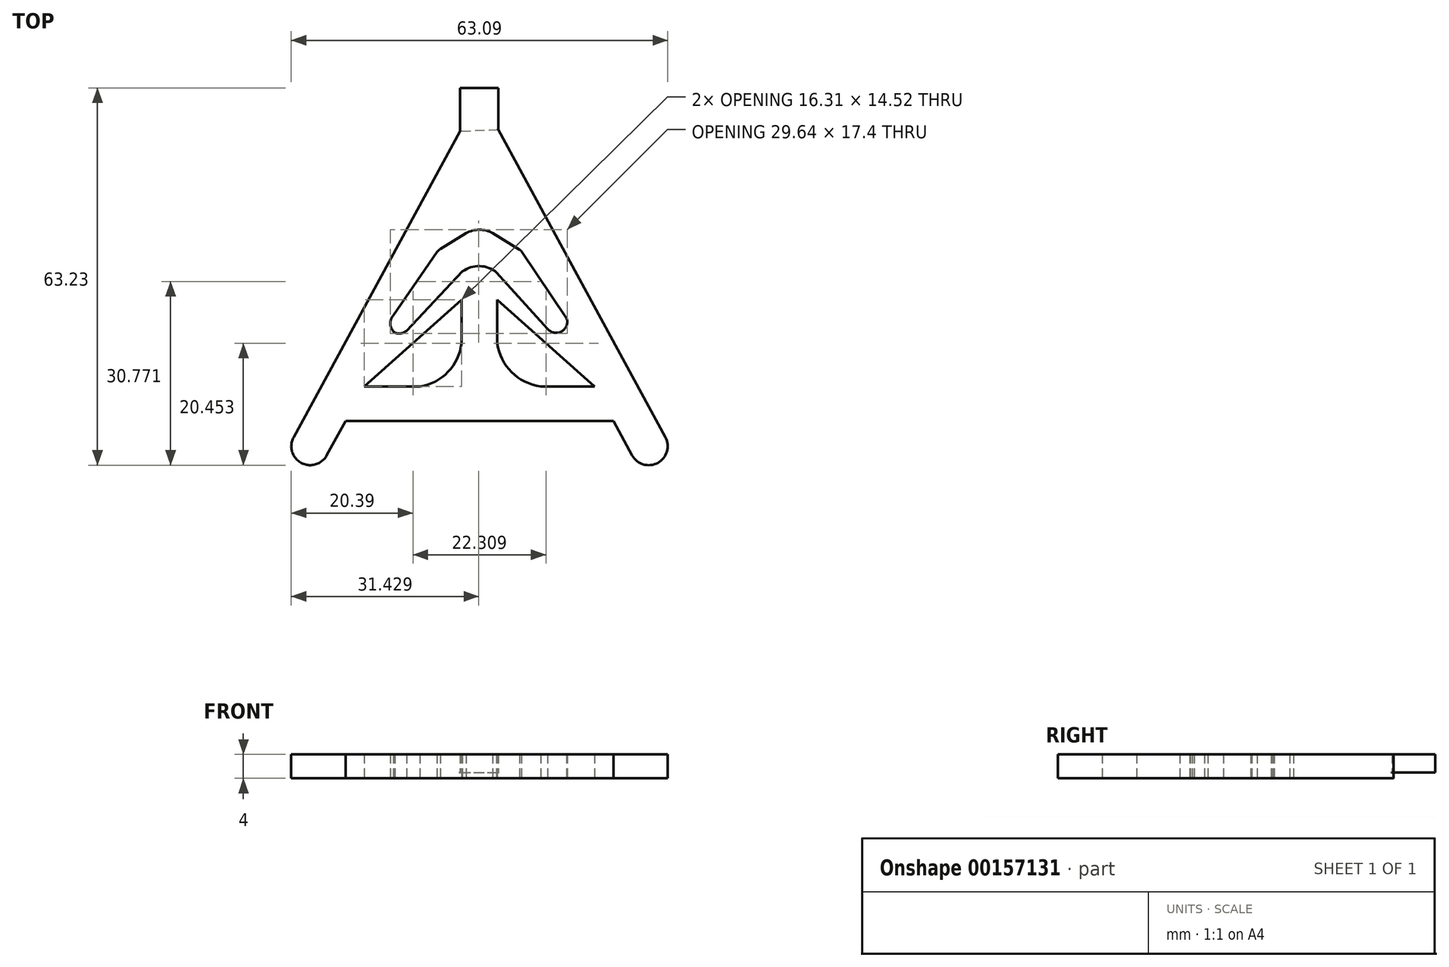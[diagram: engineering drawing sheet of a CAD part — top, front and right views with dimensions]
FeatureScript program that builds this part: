
annotation { "Feature Type Name" : "Feature", "Feature Type Description" : "" }
export const myFeature = defineFeature(function(context is Context, id is Id, definition is map)
    precondition{}
    {
        {
            var Q0;
            Q0=qCreatedBy(makeId("Top.planeOp"),FACE);
            var sketch = newSketch(context, id + "F0", { "sketchPlane" : qUnion([Q0])});
            skLineSegment(sketch, "E0", {"start": v(-31.15, 0) * mm, "end": v(-3.28, 51.3) * mm});
            skLineSegment(sketch, "E1", {"start": v(3.14, 51.54) * mm, "end": v(31.17, 0) * mm});
            skLineSegment(sketch, "E2.top", {"start": v(-3.28, 58.54) * mm, "end": v(3.14, 58.54) * mm});
            skLineSegment(sketch, "E2.left", {"start": v(-3.28, 51.3) * mm, "end": v(-3.28, 58.54) * mm});
            skLineSegment(sketch, "E2.right", {"start": v(3.14, 51.54) * mm, "end": v(3.14, 58.54) * mm});
            skPoint(sketch, "E3.orphan", {"position": v(0, 57.32) * mm});
            skLineSegment(sketch, "E4.0", {"start": v(19.31, 8.5) * mm, "end": v(25.59, -3.03) * mm});
            skLineSegment(sketch, "E4.1", {"start": v(-25.57, -3.03) * mm, "end": v(-19.3, 8.5) * mm});
            skLineSegment(sketch, "E5", {"start": v(-19.3, 8.5) * mm, "end": v(-3, 23.02) * mm});
            skLineSegment(sketch, "E6", {"start": v(3, 23.02) * mm, "end": v(19.31, 8.5) * mm});
            skPoint(sketch, "E7.start.orphan", {"position": v(-6.9, 31.34) * mm});
            skPoint(sketch, "E8.end.orphan", {"position": v(0, 35.55) * mm});
            skPoint(sketch, "E9.orphan", {"position": v(6.9, 31.34) * mm});
            skArc(sketch, "E10", {"start": v(-31.15, 0) * mm, "mid": v(-29.88, -4.3) * mm, "end": v(-25.57, -3.03) * mm});
            skArc(sketch, "E11", {"start": v(25.59, -3.03) * mm, "mid": v(29.9, -4.3) * mm, "end": v(31.17, 0) * mm});
            skLineSegment(sketch, "E12", {"start": v(-19.3, 8.5) * mm, "end": v(-9.98, 8.5) * mm});
            skLineSegment(sketch, "E13", {"start": v(22.45, 2.74) * mm, "end": v(-22.44, 2.74) * mm});
            skLineSegment(sketch, "E14", {"start": v(-3, 23.02) * mm, "end": v(-3, 15.76) * mm});
            skLineSegment(sketch, "E15", {"start": v(3, 23.02) * mm, "end": v(3, 15.76) * mm});
            skLineSegment(sketch, "E16", {"start": v(-7.1, 31.05) * mm, "end": v(-14.72, 20) * mm});
            skPoint(sketch, "E16.endSnap0", {"position": v(-9.65, 17.1) * mm});
            skLineSegment(sketch, "E17", {"start": v(-12.23, 17.86) * mm, "end": v(-2.84, 27.8) * mm});
            skLineSegment(sketch, "E18", {"start": v(2.88, 27.62) * mm, "end": v(11.53, 18.05) * mm});
            skPoint(sketch, "E18.endSnap0", {"position": v(9.66, 17.1) * mm});
            skLineSegment(sketch, "E19", {"start": v(14.62, 19.9) * mm, "end": v(7.02, 31.16) * mm});
            skLineSegment(sketch, "E20", {"start": v(2.23, 34.19) * mm, "end": v(6.75, 31.43) * mm});
            skLineSegment(sketch, "E21", {"start": v(-6.56, 31.54) * mm, "end": v(-2.24, 34.18) * mm});
            skPoint(sketch, "E22.orphan", {"position": v(0, 25.7) * mm});
            skArc(sketch, "E23", {"start": v(-9.98, 8.5) * mm, "mid": v(-5.25, 10.94) * mm, "end": v(-3, 15.76) * mm});
            skArc(sketch, "E24", {"start": v(3, 15.76) * mm, "mid": v(5.4, 10.9) * mm, "end": v(10.27, 8.5) * mm});
            skPoint(sketch, "E25.orphan", {"position": v(-3, 8.5) * mm});
            skPoint(sketch, "E26.orphan", {"position": v(3, 8.5) * mm});
            skLineSegment(sketch, "E27.trimOffspring", {"start": v(10.27, 8.5) * mm, "end": v(19.31, 8.5) * mm});
            skArc(sketch, "E28", {"start": v(-14.44, 20.41) * mm, "mid": v(-14.93, 18.9) * mm, "end": v(-14.16, 17.5) * mm});
            skArc(sketch, "E29", {"start": v(-14.16, 17.5) * mm, "mid": v(-13.15, 17.41) * mm, "end": v(-12.23, 17.86) * mm});
            skPoint(sketch, "E30.orphan", {"position": v(-16.72, 17.1) * mm});
            skArc(sketch, "E31", {"start": v(11.44, 18.14) * mm, "mid": v(13.75, 17.72) * mm, "end": v(14.62, 19.9) * mm});
            skPoint(sketch, "E32.start.orphan", {"position": v(12.39, 17.1) * mm});
            skArc(sketch, "E33", {"start": v(2.88, 27.62) * mm, "mid": v(0.05, 28.67) * mm, "end": v(-2.84, 27.8) * mm});
            skPoint(sketch, "E34.orphan", {"position": v(0, 30.8) * mm});
            skArc(sketch, "E35", {"start": v(-6.56, 31.54) * mm, "mid": v(-6.84, 31.3) * mm, "end": v(-7.1, 31.05) * mm});
            skArc(sketch, "E36", {"start": v(7.02, 31.16) * mm, "mid": v(6.9, 31.3) * mm, "end": v(6.75, 31.43) * mm});
            skArc(sketch, "E37", {"start": v(2.23, 34.19) * mm, "mid": v(0, 34.78) * mm, "end": v(-2.24, 34.18) * mm});
            skSolve(sketch);
        }
        {
            var Q0;
            Q0=makeQuery(id+"F0.imprint","IMPRINT",FACE,{"disambiguationData":[TD([[makeQuery(id+"F0.imprint","IMPRINT",EDGE,{"derivedFrom":sQuery(id+"F0.wireOp",EDGE,"E0")}),-1.0]])]});
            extrude(context, id + "F1", {"entities" : qUnion([Q0]), "depth" : 4 * mm});
        }
        {
            var Q0;
            Q0=makeQuery(id+"F1.opExtrude","CAP_FACE",FACE,{"disambiguationData":[OSD([sQuery(id+"F0.wireOp",EDGE,"E0"),sQuery(id+"F0.wireOp",EDGE,"E1"),sQuery(id+"F0.wireOp",EDGE,"E2.top"),sQuery(id+"F0.wireOp",EDGE,"E2.left"),sQuery(id+"F0.wireOp",EDGE,"E2.right"),sQuery(id+"F0.wireOp",EDGE,"E4.0"),sQuery(id+"F0.wireOp",EDGE,"E4.1"),sQuery(id+"F0.wireOp",EDGE,"E5"),sQuery(id+"F0.wireOp",EDGE,"E6"),sQuery(id+"F0.wireOp",EDGE,"E10"),sQuery(id+"F0.wireOp",EDGE,"E11"),sQuery(id+"F0.wireOp",EDGE,"E12"),sQuery(id+"F0.wireOp",EDGE,"E13"),sQuery(id+"F0.wireOp",EDGE,"E14"),sQuery(id+"F0.wireOp",EDGE,"E15"),sQuery(id+"F0.wireOp",EDGE,"E16"),sQuery(id+"F0.wireOp",EDGE,"E17"),sQuery(id+"F0.wireOp",EDGE,"E18"),sQuery(id+"F0.wireOp",EDGE,"E19"),sQuery(id+"F0.wireOp",EDGE,"E20"),sQuery(id+"F0.wireOp",EDGE,"E21"),sQuery(id+"F0.wireOp",EDGE,"E23"),sQuery(id+"F0.wireOp",EDGE,"E24"),sQuery(id+"F0.wireOp",EDGE,"E27.trimOffspring"),sQuery(id+"F0.wireOp",EDGE,"E28"),sQuery(id+"F0.wireOp",EDGE,"E29"),sQuery(id+"F0.wireOp",EDGE,"E31"),sQuery(id+"F0.wireOp",EDGE,"E33"),sQuery(id+"F0.wireOp",EDGE,"E35"),sQuery(id+"F0.wireOp",EDGE,"E36"),sQuery(id+"F0.wireOp",EDGE,"E37")])],"isStart":true});
            var sketch = newSketch(context, id + "F2", { "sketchPlane" : qUnion([Q0])});
            skLineSegment(sketch, "E38", {"start": v(-3.28, -51.3) * mm, "end": v(3.14, -51.54) * mm});
            skSolve(sketch);
        }
        {
            var Q0;
            Q0=makeQuery(id+"F2.imprint","IMPRINT",FACE,{"disambiguationData":[TD([[makeQuery(id+"F2.imprint","IMPRINT",EDGE,{"derivedFrom":sQuery(id+"F2.wireOp",EDGE,"E38")}),-1.0]])]});
            extrude(context, id + "F3", {"entities" : qUnion([Q0]), "operationType" : NewBodyOperationType.REMOVE, "oppositeDirection" : true, "depth" : 1 * mm});
        }
        {
            var Q0;
            Q0=makeQuery(id+"F3.boolean.opBoolean","COPY",EDGE,{"derivedFrom":makeQuery(id+"F3.opExtrude","CAP_EDGE",EDGE,{"disambiguationData":[OSD([sQuery(id+"F2.wireOp",EDGE,"E38")])],"isStart":true})});
            var Q1;
            {var subQ0=sQuery(id+"F0.wireOp",EDGE,"E2.right");var subQ1=sQuery(id+"F0.wireOp",EDGE,"E1");Q1=makeQuery(id+"F3.boolean.opBoolean","MERGE",EDGE,{"derivedFrom":[makeQuery(id+"F1.opExtrude","SWEPT_EDGE",EDGE,{"disambiguationData":[OSD([subQ1,subQ0])]}),makeQuery(id+"F3.opExtrude","SWEPT_EDGE",EDGE,{"disambiguationData":[OSD([subQ1,subQ0,sQuery(id+"F2.wireOp",EDGE,"E38")])]})]});}
            var Q2;
            {var subQ0=sQuery(id+"F0.wireOp",EDGE,"E2.left");var subQ1=sQuery(id+"F0.wireOp",EDGE,"E0");Q2=makeQuery(id+"F3.boolean.opBoolean","MERGE",EDGE,{"derivedFrom":[makeQuery(id+"F1.opExtrude","SWEPT_EDGE",EDGE,{"disambiguationData":[OSD([subQ1,subQ0])]}),makeQuery(id+"F3.opExtrude","SWEPT_EDGE",EDGE,{"disambiguationData":[OSD([subQ1,subQ0,sQuery(id+"F2.wireOp",EDGE,"E38")])]})]});}
            var Q3;
            Q3=makeQuery(id+"F3.boolean.opBoolean","COPY",EDGE,{"derivedFrom":makeQuery(id+"F3.opExtrude","CAP_EDGE",EDGE,{"disambiguationData":[OSD([sQuery(id+"F0.wireOp",EDGE,"E2.right")])],"isStart":false})});
            var Q4;
            Q4=makeQuery(id+"F3.boolean.opBoolean","COPY",EDGE,{"derivedFrom":makeQuery(id+"F3.opExtrude","CAP_EDGE",EDGE,{"disambiguationData":[OSD([sQuery(id+"F0.wireOp",EDGE,"E2.left")])],"isStart":false})});
            var Q5;
            Q5=makeQuery(id+"F3.boolean.opBoolean","COPY",EDGE,{"derivedFrom":makeQuery(id+"F3.opExtrude","CAP_EDGE",EDGE,{"disambiguationData":[OSD([sQuery(id+"F0.wireOp",EDGE,"E2.top")])],"isStart":false})});
            fillet(context, id + "F4", {"entities" : qUnion([Q0, Q1, Q2, Q3, Q4, Q5]), "radius" : 0.5 * mm, "tangentPropagation" : true, "allowEdgeOverflow" : false});
        }
    });
